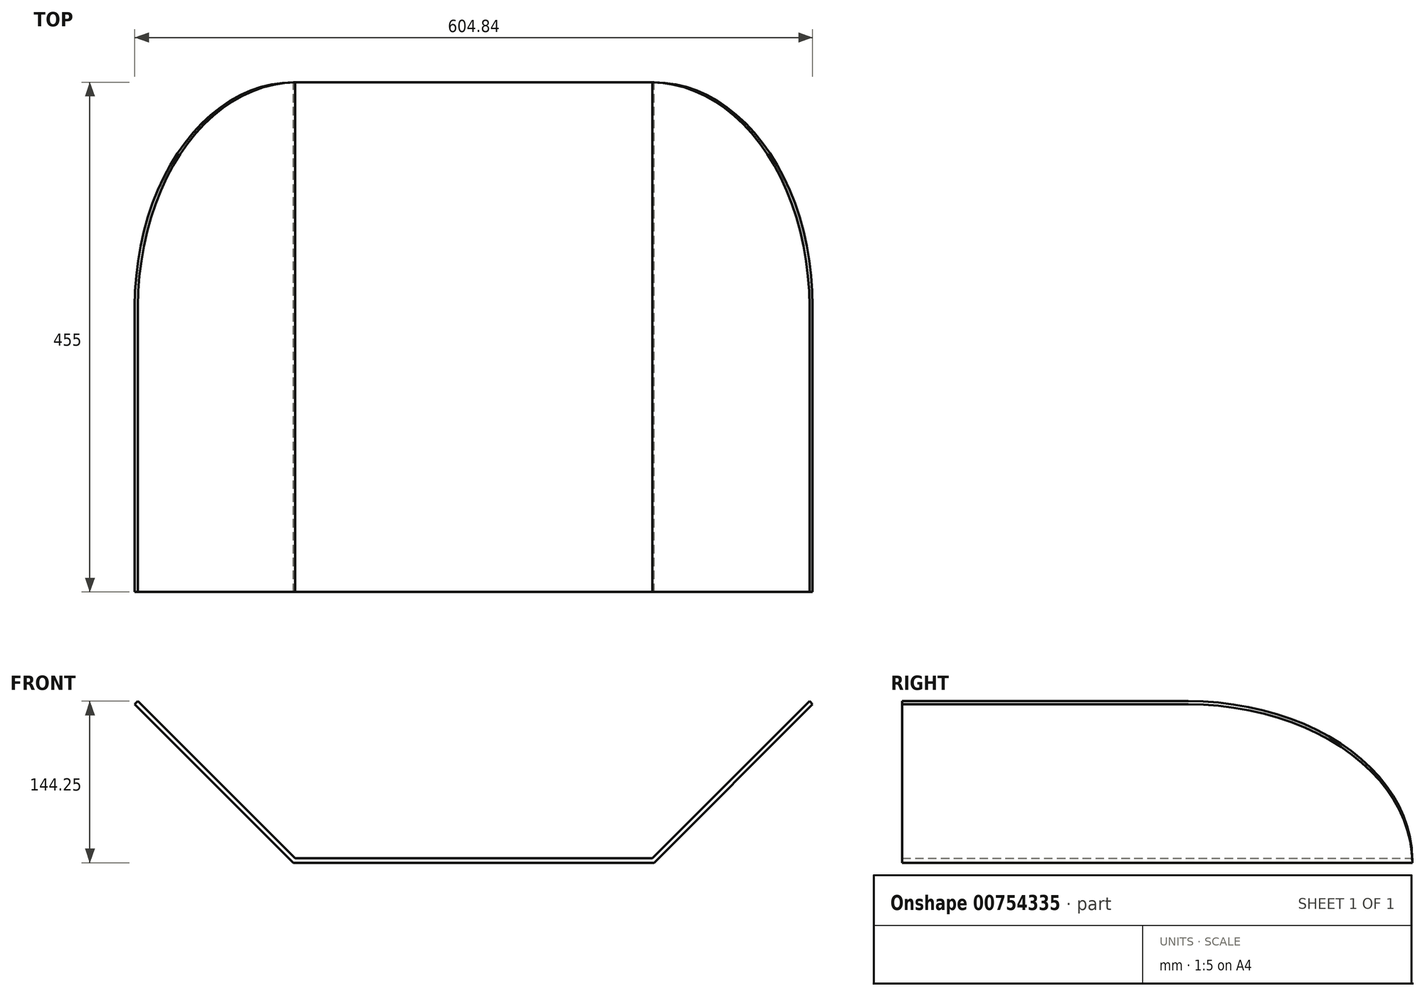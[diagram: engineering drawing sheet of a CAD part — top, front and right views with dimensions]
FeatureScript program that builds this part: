
annotation { "Feature Type Name" : "Feature", "Feature Type Description" : "" }
export const myFeature = defineFeature(function(context is Context, id is Id, definition is map)
    precondition{}
    {
        {
            var Q0;
            Q0=qCreatedBy(makeId("Front.planeOp"),FACE);
            var sketch = newSketch(context, id + "F0", { "sketchPlane" : qUnion([Q0])});
            skLineSegment(sketch, "E0", {"start": v(0, 0) * mm, "end": v(161, 0) * mm});
            skLineSegment(sketch, "E1", {"start": v(161, 0) * mm, "end": v(302.42, 141.42) * mm});
            skLineSegment(sketch, "E2", {"start": v(302.42, 141.42) * mm, "end": v(299.6, 144.25) * mm});
            skLineSegment(sketch, "E3", {"start": v(299.6, 144.25) * mm, "end": v(159.34, 4) * mm});
            skLineSegment(sketch, "E4", {"start": v(159.34, 4) * mm, "end": v(0, 4) * mm});
            skLineSegment(sketch, "E5", {"start": v(0, 4) * mm, "end": v(-159.34, 4) * mm});
            skLineSegment(sketch, "E6", {"start": v(-159.34, 4) * mm, "end": v(-299.6, 144.25) * mm});
            skLineSegment(sketch, "E7", {"start": v(-299.6, 144.25) * mm, "end": v(-302.42, 141.42) * mm});
            skLineSegment(sketch, "E8", {"start": v(-302.42, 141.42) * mm, "end": v(-161, 0) * mm});
            skLineSegment(sketch, "E9", {"start": v(-161, 0) * mm, "end": v(0, 0) * mm});
            skSolve(sketch);
        }
        {
            var Q0;
            Q0 = qSketchRegion(id + "F0", true);
            extrude(context, id + "F1", {"entities" : qUnion([Q0]), "depth" : 255 * mm, "offsetDistance" : 25 * mm});
        }
        {
            var Q0;
            Q0=makeQuery(id+"F1.opExtrude","CAP_FACE",FACE,{"disambiguationData":[OSD([sQuery(id+"F0.wireOp",EDGE,"E0"),sQuery(id+"F0.wireOp",EDGE,"E1"),sQuery(id+"F0.wireOp",EDGE,"E2"),sQuery(id+"F0.wireOp",EDGE,"E3"),sQuery(id+"F0.wireOp",EDGE,"E4"),sQuery(id+"F0.wireOp",EDGE,"E5"),sQuery(id+"F0.wireOp",EDGE,"E6"),sQuery(id+"F0.wireOp",EDGE,"E7"),sQuery(id+"F0.wireOp",EDGE,"E8"),sQuery(id+"F0.wireOp",EDGE,"E9")])],"isStart":true});
            var sketch = newSketch(context, id + "F2", { "sketchPlane" : qUnion([Q0])});
            skLineSegment(sketch, "E10", {"start": v(-299.6, 144.25) * mm, "end": v(-302.42, 141.42) * mm});
            skLineSegment(sketch, "E11", {"start": v(-302.42, 141.42) * mm, "end": v(-161, 0) * mm});
            skLineSegment(sketch, "E12", {"start": v(-161, 0) * mm, "end": v(161, 0) * mm});
            skLineSegment(sketch, "E13", {"start": v(161, 0) * mm, "end": v(302.42, 141.42) * mm});
            skLineSegment(sketch, "E14", {"start": v(302.42, 141.42) * mm, "end": v(299.6, 144.25) * mm});
            skLineSegment(sketch, "E15", {"start": v(299.6, 144.25) * mm, "end": v(159.34, 4) * mm});
            skLineSegment(sketch, "E16", {"start": v(159.34, 4) * mm, "end": v(-159.34, 4) * mm});
            skLineSegment(sketch, "E17", {"start": v(-159.34, 4) * mm, "end": v(-299.6, 144.25) * mm});
            skSolve(sketch);
        }
        {
            var Q0;
            Q0 = qSketchRegion(id + "F2", true);
            extrude(context, id + "F3", {"entities" : qUnion([Q0]), "operationType" : NewBodyOperationType.ADD, "depth" : 200 * mm, "offsetDistance" : 25 * mm});
        }
        {
            var Q0;
            Q0=makeQuery(id+"F3.opExtrude","CAP_EDGE",EDGE,{"disambiguationData":[OSD([sQuery(id+"F2.wireOp",EDGE,"E10")])],"isStart":false});
            fillet(context, id + "F4", {"entities" : qUnion([Q0]), "radius" : 200 * mm, "tangentPropagation" : true, "allowEdgeOverflow" : false});
        }
        {
            var Q0;
            Q0=makeQuery(id+"F3.opExtrude","CAP_EDGE",EDGE,{"disambiguationData":[OSD([sQuery(id+"F2.wireOp",EDGE,"E14")])],"isStart":false});
            fillet(context, id + "F5", {"entities" : qUnion([Q0]), "radius" : 200 * mm, "tangentPropagation" : true, "allowEdgeOverflow" : false});
        }
    });
